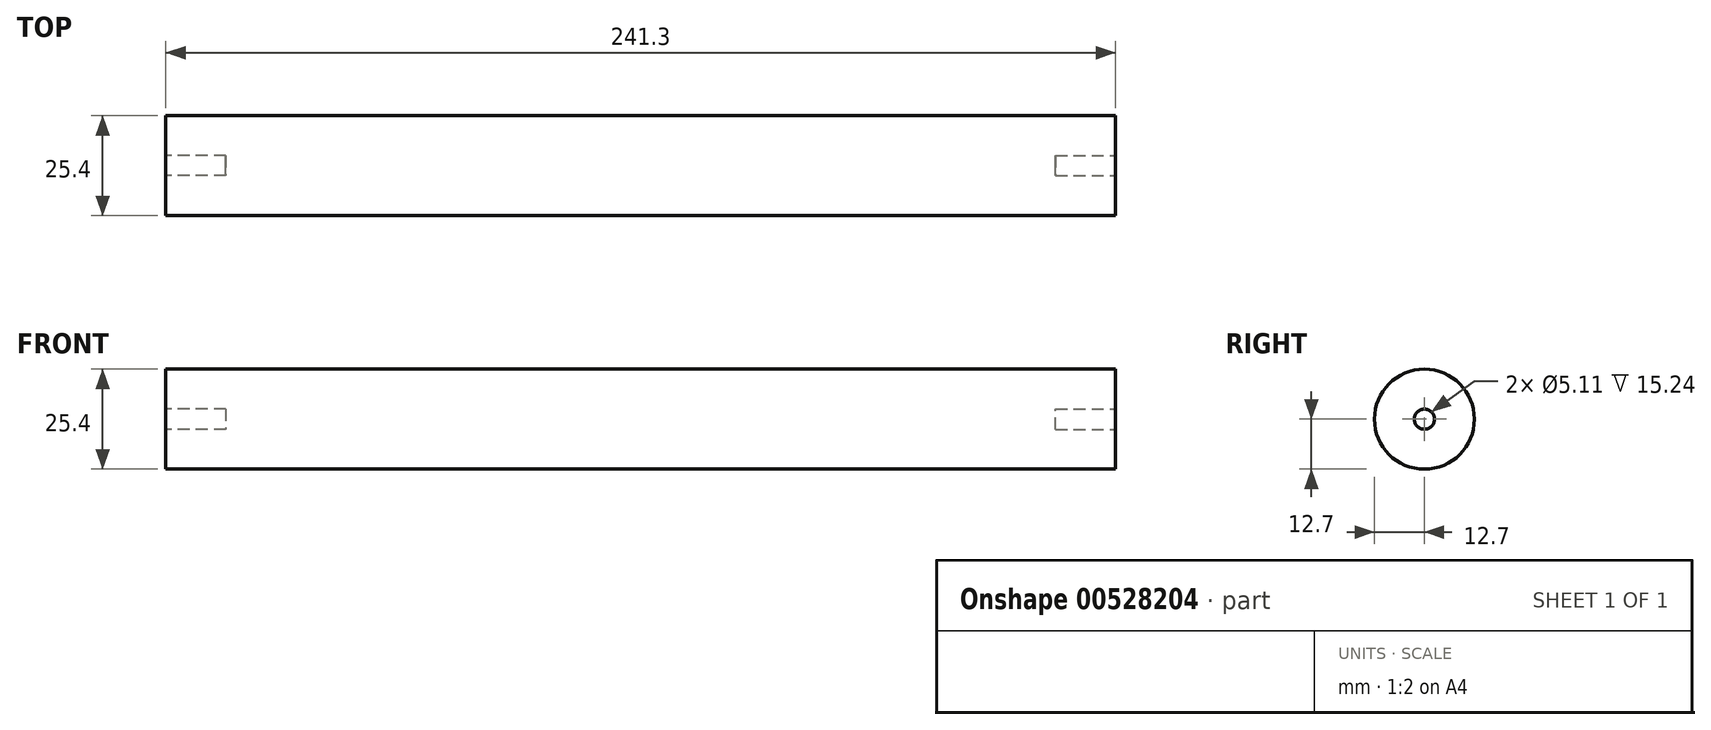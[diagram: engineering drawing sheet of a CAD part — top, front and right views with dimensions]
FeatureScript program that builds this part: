
annotation { "Feature Type Name" : "Feature", "Feature Type Description" : "" }
export const myFeature = defineFeature(function(context is Context, id is Id, definition is map)
    precondition{}
    {
        {
            var Q0;
            Q0=qCreatedBy(makeId("Right.planeOp"),FACE);
            var sketch = newSketch(context, id + "F0", { "sketchPlane" : qUnion([Q0])});
            skCircle(sketch, "E0", {"center": v(0, 0) * mm, "radius": 12.7 * mm});
            skSolve(sketch);
        }
        {
            var Q0;
            Q0 = qSketchRegion(id + "F0", true);
            extrude(context, id + "F1", {"entities" : qUnion([Q0]), "depth" : 241.3 * mm, "offsetDistance" : 25.4 * mm});
        }
        {
            var Q0;
            Q0=makeQuery(id+"F1.opExtrude","CAP_FACE",FACE,{"disambiguationData":[OSD([sQuery(id+"F0.wireOp",EDGE,"E0")])],"isStart":false});
            var sketch = newSketch(context, id + "F2", { "sketchPlane" : qUnion([Q0])});
            skCircle(sketch, "E1", {"center": v(0, 0) * mm, "radius": 2.55 * mm});
            skSolve(sketch);
        }
        {
            var Q0;
            Q0 = qSketchRegion(id + "F2", true);
            var Q1;
            Q1 = qSketchRegion(id + "F0", true);
            extrude(context, id + "F3", {"entities" : qUnion([Q0, Q1]), "operationType" : NewBodyOperationType.REMOVE, "oppositeDirection" : true, "depth" : 15.24 * mm, "offsetDistance" : 25.4 * mm});
        }
        {
            var Q0;
            Q0=makeQuery(id+"F1.opExtrude","CAP_FACE",FACE,{"disambiguationData":[OSD([sQuery(id+"F0.wireOp",EDGE,"E0")])],"isStart":true});
            var sketch = newSketch(context, id + "F4", { "sketchPlane" : qUnion([Q0])});
            skCircle(sketch, "E2.0", {"center": v(0, 0) * mm, "radius": 2.55 * mm});
            skSolve(sketch);
        }
        {
            var Q0;
            Q0 = qSketchRegion(id + "F4", true);
            extrude(context, id + "F5", {"entities" : qUnion([Q0]), "operationType" : NewBodyOperationType.REMOVE, "oppositeDirection" : true, "depth" : 15.24 * mm, "offsetDistance" : 25.4 * mm});
        }
    });
